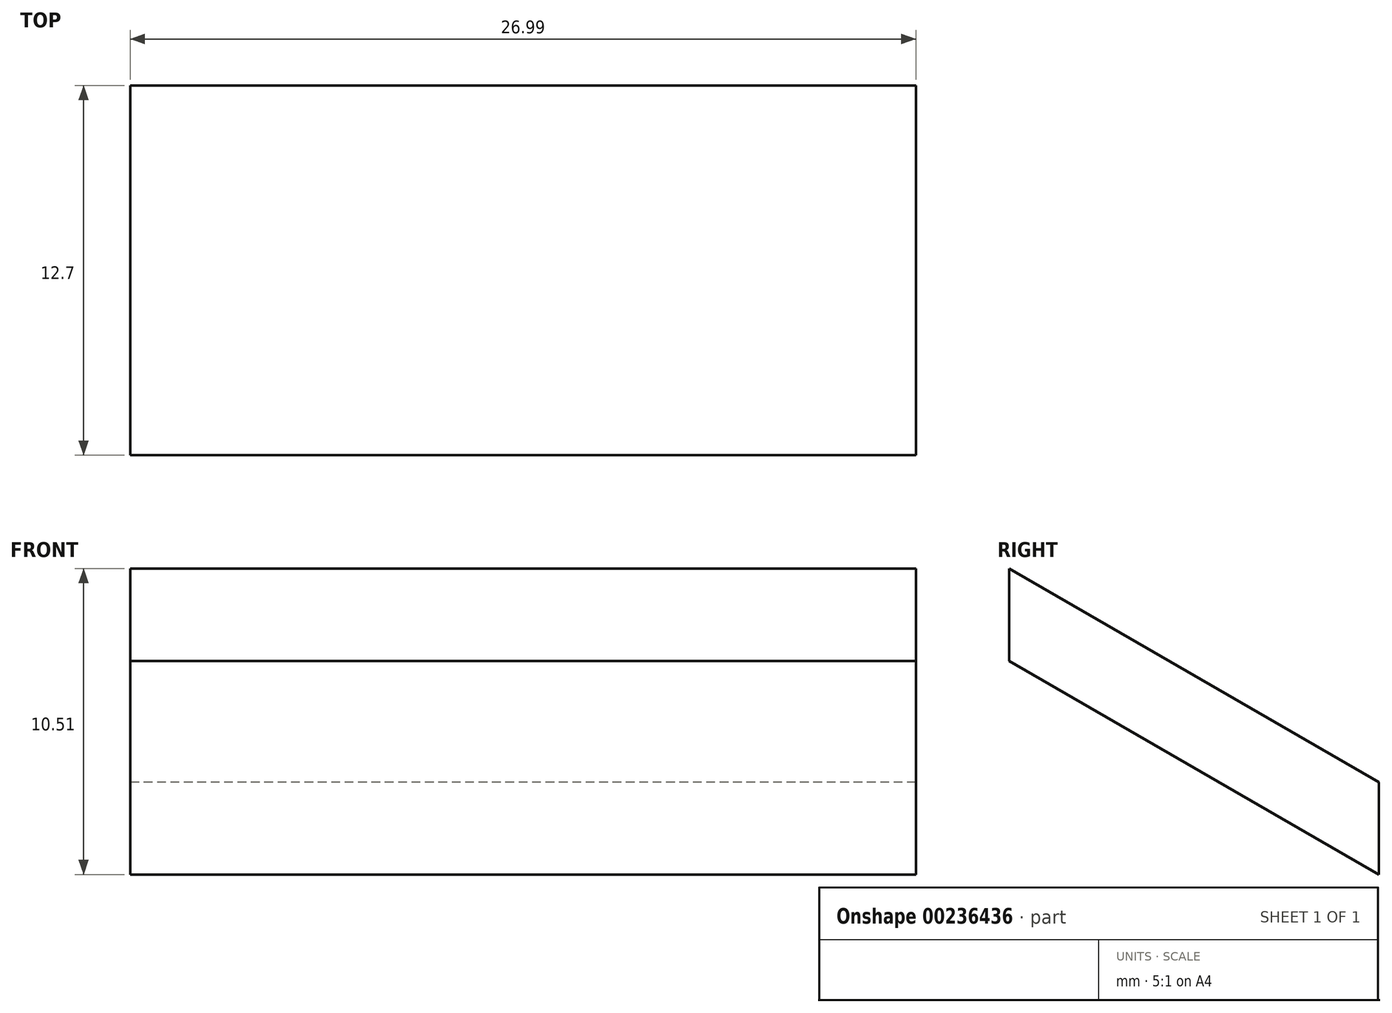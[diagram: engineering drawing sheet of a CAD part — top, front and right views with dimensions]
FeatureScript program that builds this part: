
annotation { "Feature Type Name" : "Feature", "Feature Type Description" : "" }
export const myFeature = defineFeature(function(context is Context, id is Id, definition is map)
    precondition{}
    {
        {
            var Q0;
            Q0=qCreatedBy(makeId("Right.planeOp"),FACE);
            var sketch = newSketch(context, id + "F0", { "sketchPlane" : qUnion([Q0])});
            skLineSegment(sketch, "E0", {"start": v(24.52, -12.94) * mm, "end": v(24.52, -16.12) * mm});
            skLineSegment(sketch, "E1", {"start": v(24.52, -16.12) * mm, "end": v(11.82, -8.79) * mm});
            skLineSegment(sketch, "E2", {"start": v(24.52, -12.94) * mm, "end": v(11.82, -5.61) * mm});
            skLineSegment(sketch, "E3", {"start": v(11.82, -8.79) * mm, "end": v(11.82, -5.61) * mm});
            skSolve(sketch);
        }
        {
            var Q0;
            Q0 = qSketchRegion(id + "F0", true);
            extrude(context, id + "F1", {"entities" : qUnion([Q0]), "depth" : 26.99 * mm});
        }
    });
